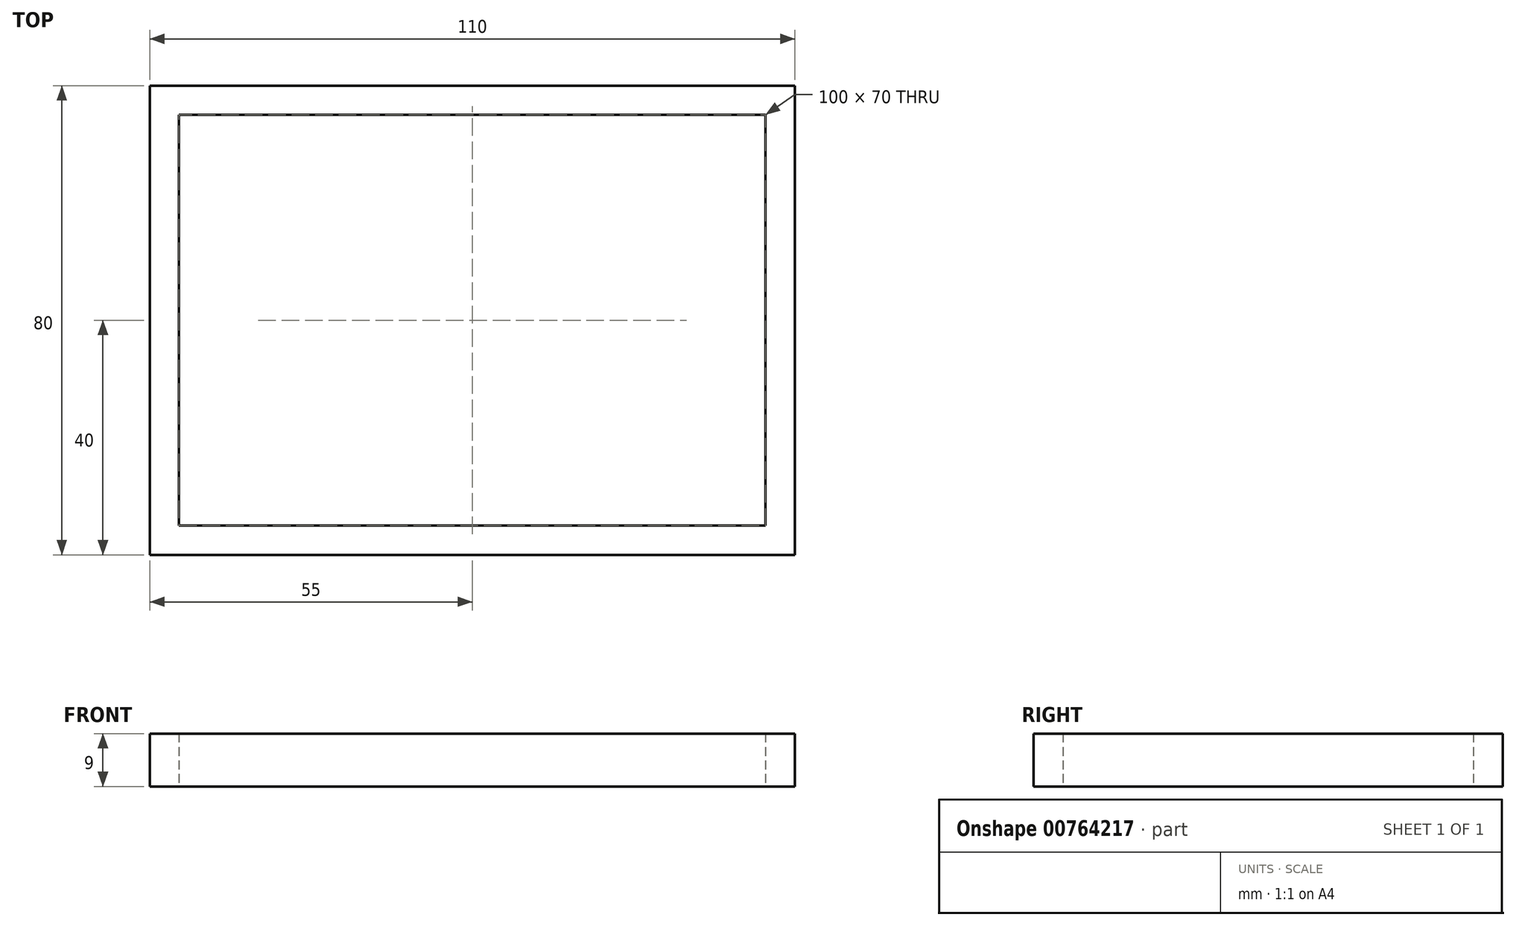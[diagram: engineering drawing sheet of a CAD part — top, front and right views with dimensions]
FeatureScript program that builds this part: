
annotation { "Feature Type Name" : "Feature", "Feature Type Description" : "" }
export const myFeature = defineFeature(function(context is Context, id is Id, definition is map)
    precondition{}
    {
        {
            var Q0;
            Q0=qCreatedBy(makeId("Top.planeOp"),FACE);
            var sketch = newSketch(context, id + "F0", { "sketchPlane" : qUnion([Q0])});
            skLineSegment(sketch, "E0.bottom", {"start": v(0, 0) * mm, "end": v(110, 0) * mm});
            skLineSegment(sketch, "E0.top", {"start": v(0, 80) * mm, "end": v(110, 80) * mm});
            skLineSegment(sketch, "E0.left", {"start": v(0, 0) * mm, "end": v(0, 80) * mm});
            skLineSegment(sketch, "E0.right", {"start": v(110, 0) * mm, "end": v(110, 80) * mm});
            skLineSegment(sketch, "E1.bottom", {"start": v(5, 5) * mm, "end": v(105, 5) * mm});
            skLineSegment(sketch, "E1.top", {"start": v(5, 75) * mm, "end": v(105, 75) * mm});
            skLineSegment(sketch, "E1.left", {"start": v(5, 5) * mm, "end": v(5, 75) * mm});
            skLineSegment(sketch, "E1.right", {"start": v(105, 5) * mm, "end": v(105, 75) * mm});
            skSolve(sketch);
        }
        {
            var Q0;
            Q0=makeQuery(id+"F0.imprint","IMPRINT",FACE,{"disambiguationData":[TD([[makeQuery(id+"F0.imprint","IMPRINT",EDGE,{"derivedFrom":sQuery(id+"F0.wireOp",EDGE,"E0.bottom")}),1.0]])]});
            extrude(context, id + "F1", {"entities" : qUnion([Q0]), "depth" : 9 * mm, "offsetDistance" : 25 * mm});
        }
    });
